# Revit family: DTI_A3-Fold-A-Side-3-Door-SD11
name_source: partatom
category: Doors
revit_build: Autodesk Revit 2016 (Build: 20150220_1215(x64)
units: mm (PartAtom-declared; Revit-internal decimal feet)

## family parameters
Always vertical = Yes
Cut with Voids When Loaded = No
Host = Wall
OmniClass Number = 23.30.10.00
OmniClass Title = Doors
Room Calculation Point = No
Shared = No

## types (1)
- Fold A Side 3 Door SD11
    Cill Height = 20 mm  [stored 0.0656168 ft]
    Description = Fold a Side 3 Door SD11
    Door Frame Material = Meranti
    Door Height = 2032 mm
    Door Material = Meranti
    Door Width = 813 mm
    Frame Depth = 83 mm  [stored 0.27231 ft]
    Frame Width = 68 mm
    Function = Exterior
    Height = 2100 mm
    Manufacturer = Swartland Doors & Windows
    Model = Fold a Side 3 Door SD11
    Rough Height = 2518 mm  [stored 8.26115 ft]
    Rough Width = 961 mm
    URL = www.swartland.co.za
    Wall Closure = By host
    Width = 2570 mm  [stored 8.43176 ft]

note: [stored X ft] marks values corroborated as IEEE doubles in the binary element streams (Revit-internal decimal feet)

## geometry (parser evidence)
native form markers: Blend x18, Sweep x10
no freeform markers — native parametric forms only
